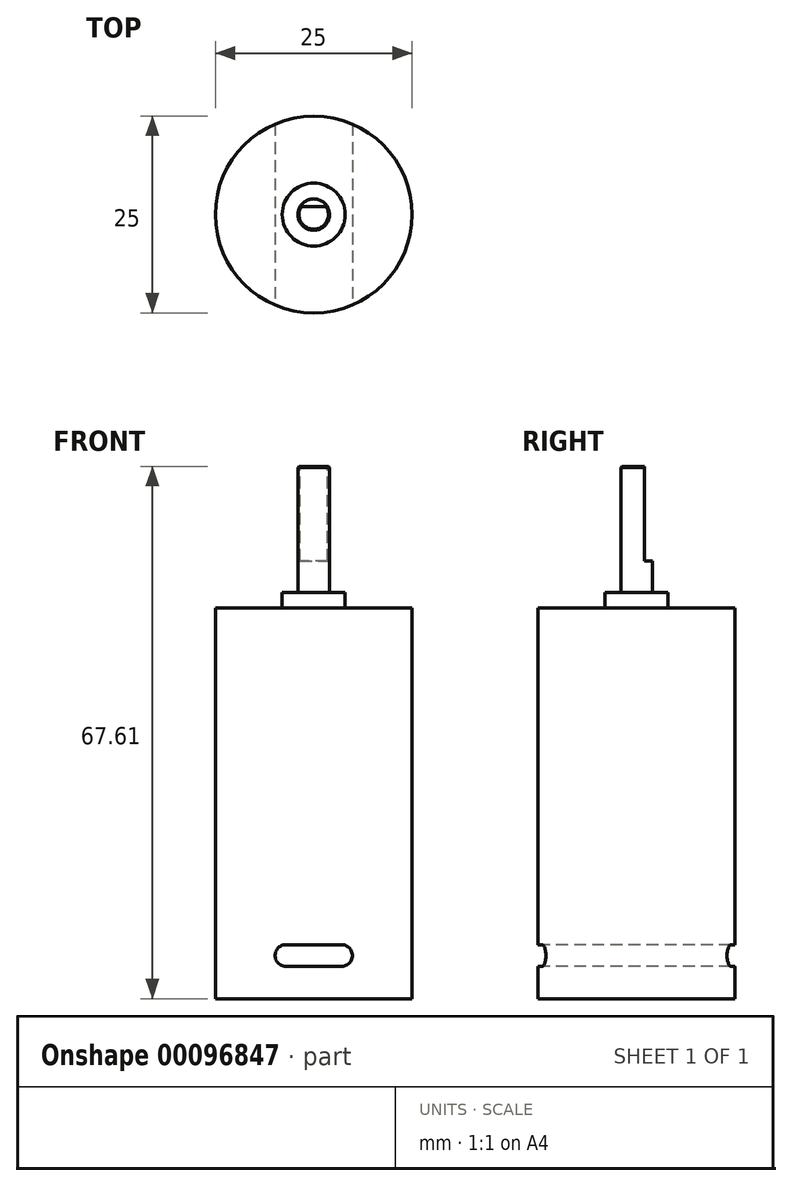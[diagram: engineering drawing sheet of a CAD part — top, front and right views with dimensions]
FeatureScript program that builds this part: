
annotation { "Feature Type Name" : "Feature", "Feature Type Description" : "" }
export const myFeature = defineFeature(function(context is Context, id is Id, definition is map)
    precondition{}
    {
        {
            var Q0;
            Q0=qCreatedBy(makeId("Right.planeOp"),FACE);
            var sketch = newSketch(context, id + "F0", { "sketchPlane" : qUnion([Q0])});
            skLineSegment(sketch, "E0", {"start": v(0, 0) * mm, "end": v(12.5, 0) * mm});
            skLineSegment(sketch, "E1", {"start": v(12.5, 0) * mm, "end": v(12.5, 49.6) * mm});
            skLineSegment(sketch, "E2", {"start": v(12.5, 49.6) * mm, "end": v(4, 49.6) * mm});
            skLineSegment(sketch, "E3", {"start": v(4, 49.6) * mm, "end": v(4, 51.61) * mm});
            skLineSegment(sketch, "E4", {"start": v(4, 51.61) * mm, "end": v(2, 51.61) * mm});
            skLineSegment(sketch, "E5", {"start": v(2, 51.61) * mm, "end": v(2, 67.61) * mm});
            skLineSegment(sketch, "E6", {"start": v(2, 67.61) * mm, "end": v(0, 67.61) * mm});
            skLineSegment(sketch, "E7", {"start": v(0, 67.6) * mm, "end": v(0, 0) * mm});
            skSolve(sketch);
        }
        {
            var Q0;
            Q0=makeQuery(id+"F0.imprint","IMPRINT",FACE,{"disambiguationData":[TD([[makeQuery(id+"F0.imprint","IMPRINT",EDGE,{"derivedFrom":sQuery(id+"F0.wireOp",EDGE,"E0")}),1.0]])]});
            var Q1;
            Q1=sQuery(id+"F0.wireOp",EDGE,"E7");
            revolve(context, id + "F1", {"entities" : qUnion([Q0]), "axis" : qUnion([Q1]), "revolveType" : RevolveType.FULL});
        }
        {
            var Q0;
            Q0=makeQuery(id+"F1.opRevolve","SWEPT_FACE",FACE,{"disambiguationData":[OSD([sQuery(id+"F0.wireOp",EDGE,"E6")])]});
            var sketch = newSketch(context, id + "F2", { "sketchPlane" : qUnion([Q0])});
            skLineSegment(sketch, "E8.bottom", {"start": v(-1.73, 1) * mm, "end": v(1.73, 1) * mm});
            skLineSegment(sketch, "E8.top", {"start": v(-1.73, 2) * mm, "end": v(1.73, 2) * mm});
            skLineSegment(sketch, "E8.left", {"start": v(-1.73, 1) * mm, "end": v(-1.73, 2) * mm});
            skLineSegment(sketch, "E8.right", {"start": v(1.73, 1) * mm, "end": v(1.73, 2) * mm});
            skSolve(sketch);
        }
        {
            var Q0;
            Q0 = qSketchRegion(id + "F2", true);
            extrude(context, id + "F3", {"entities" : qUnion([Q0]), "operationType" : NewBodyOperationType.REMOVE, "oppositeDirection" : true, "depth" : 12 * mm});
        }
        {
            var Q0;
            Q0=makeQuery(id+"F1.opRevolve","SWEPT_EDGE",EDGE,{"disambiguationData":[OSD([sQuery(id+"F0.wireOp",EDGE,"E5"),sQuery(id+"F0.wireOp",EDGE,"E6")])]});
            chamfer(context, id + "F4", {"entities" : qUnion([Q0]), "width" : 0.13 * mm, "tangentPropagation" : true});
        }
        {
            var Q0;
            Q0=qCreatedBy(makeId("Front.planeOp"),FACE);
            var sketch = newSketch(context, id + "F5", { "sketchPlane" : qUnion([Q0])});
            skLineSegment(sketch, "E9.bottom", {"start": v(-3.52, 6.86) * mm, "end": v(3.52, 6.86) * mm});
            skLineSegment(sketch, "E9.top", {"start": v(-3.52, 4.09) * mm, "end": v(3.52, 4.09) * mm});
            skLineSegment(sketch, "E9.left", {"start": v(-3.52, 6.86) * mm, "end": v(-3.52, 4.09) * mm});
            skLineSegment(sketch, "E9.right", {"start": v(3.52, 6.86) * mm, "end": v(3.52, 4.09) * mm});
            skCircle(sketch, "E10", {"center": v(-3.52, 5.47) * mm, "radius": 1.38 * mm});
            skCircle(sketch, "E11", {"center": v(3.52, 5.47) * mm, "radius": 1.38 * mm});
            skLineSegment(sketch, "E12", {"start": v(0, -0.48) * mm, "end": v(0, 4.09) * mm, "construction": true});
            skSolve(sketch);
        }
        {
            var Q0;
            Q0 = qSketchRegion(id + "F5", true);
            extrude(context, id + "F6", {"entities" : qUnion([Q0]), "operationType" : NewBodyOperationType.REMOVE, "endBound" : BoundingType.SYMMETRIC, "oppositeDirection" : true, "depth" : 152.4 * mm});
        }
    });
